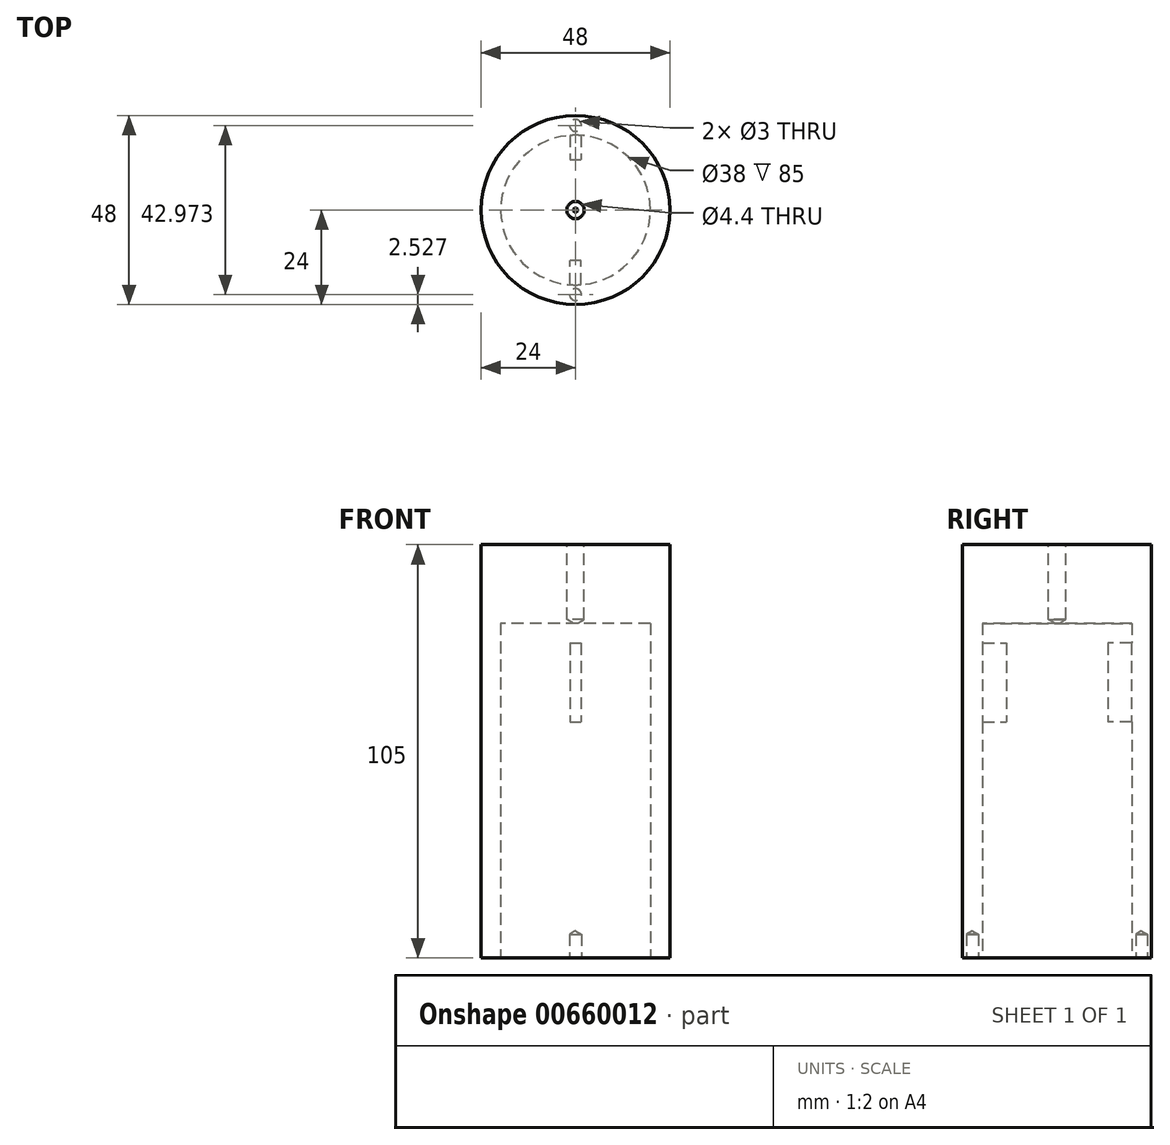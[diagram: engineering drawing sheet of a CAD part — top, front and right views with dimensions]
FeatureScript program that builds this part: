
annotation { "Feature Type Name" : "Feature", "Feature Type Description" : "" }
export const myFeature = defineFeature(function(context is Context, id is Id, definition is map)
    precondition{}
    {
        {
            var Q0;
            Q0=qCreatedBy(makeId("Top.planeOp"),FACE);
            var sketch = newSketch(context, id + "F0", { "sketchPlane" : qUnion([Q0])});
            skCircle(sketch, "E0", {"center": v(0, 0) * mm, "radius": 15.25 * mm});
            skPoint(sketch, "E1", {"position": v(-15.25, 0) * mm});
            skPoint(sketch, "E2", {"position": v(15.25, 0) * mm});
            skArc(sketch, "E3", {"start": v(14.87, 3.38) * mm, "mid": v(18.65, 0) * mm, "end": v(14.87, -3.38) * mm});
            skArc(sketch, "E4", {"start": v(-14.87, 3.38) * mm, "mid": v(-18.65, 0) * mm, "end": v(-14.87, -3.38) * mm});
            skCircle(sketch, "E5", {"center": v(0, 0) * mm, "radius": 19 * mm});
            skCircle(sketch, "E6", {"center": v(0, 0) * mm, "radius": 24 * mm});
            skPoint(sketch, "E7", {"position": v(12.03, 14.7) * mm});
            skPoint(sketch, "E8", {"position": v(-16.68, 9.1) * mm});
            skLineSegment(sketch, "E9", {"start": v(-1.44, -18.95) * mm, "end": v(-1.44, -12.87) * mm});
            skLineSegment(sketch, "E10", {"start": v(-1.44, -12.87) * mm, "end": v(0, -12.87) * mm});
            skLineSegment(sketch, "E11.MirrorCS", {"start": v(1.44, -18.95) * mm, "end": v(1.44, -12.87) * mm});
            skLineSegment(sketch, "E12.MirrorCS", {"start": v(1.44, -12.87) * mm, "end": v(0, -12.87) * mm});
            skLineSegment(sketch, "E13.MirrorCS", {"start": v(-1.44, 18.95) * mm, "end": v(-1.44, 12.87) * mm});
            skLineSegment(sketch, "E14.MirrorCS", {"start": v(-1.44, 12.87) * mm, "end": v(0, 12.87) * mm});
            skLineSegment(sketch, "E15.MirrorCS", {"start": v(1.44, 12.87) * mm, "end": v(0, 12.87) * mm});
            skLineSegment(sketch, "E16.MirrorCS", {"start": v(1.44, 18.95) * mm, "end": v(1.44, 12.87) * mm});
            skPoint(sketch, "E17", {"position": v(0, -18.95) * mm});
            skPoint(sketch, "E18", {"position": v(0, 19) * mm});
            skLineSegment(sketch, "E19", {"start": v(0, -18.95) * mm, "end": v(0, -24) * mm});
            skLineSegment(sketch, "E20", {"start": v(0, 19) * mm, "end": v(0, 24) * mm});
            skPoint(sketch, "E21", {"position": v(0, -21.47) * mm});
            skPoint(sketch, "E22", {"position": v(0, 21.5) * mm});
            skSolve(sketch);
        }
        {
            var Q0;
            Q0=makeQuery(id+"F0.imprint","IMPRINT",FACE,{"disambiguationData":[TD([[makeQuery(id+"F0.imprint","IMPRINT",EDGE,{"derivedFrom":sQuery(id+"F0.wireOp",EDGE,"E6")}),1.0]])]});
            extrude(context, id + "F1", {"entities" : qUnion([Q0]), "depth" : 1 * mm, "offsetDistance" : 25 * mm});
        }
        {
            var Q0;
            Q0=makeQuery(id+"F0.imprint","IMPRINT",FACE,{"disambiguationData":[TD([[makeQuery(id+"F0.imprint","IMPRINT",EDGE,{"derivedFrom":sQuery(id+"F0.wireOp",EDGE,"E5")}),-1.0]])]});
            extrude(context, id + "F2", {"entities" : qUnion([Q0]), "operationType" : NewBodyOperationType.ADD, "depth" : 85 * mm, "offsetDistance" : 25 * mm});
        }
        {
            var Q0;
            {var subQ0=sQuery(id+"F0.wireOp",EDGE,"E3");var subQ1=sQuery(id+"F0.wireOp",EDGE,"E0");var subQ2=makeQuery(id+"F0.imprint","INTERSECT",VERTEX,{"disambiguationData":[OD(0.0)],"derivedFrom":[subQ1,subQ0]});Q0=makeQuery(id+"F0.imprint","IMPRINT",FACE,{"disambiguationData":[TD([[makeQuery(id+"F0.imprint","IMPRINT",EDGE,{"disambiguationData":[TD([[subQ2,-1.0]])],"derivedFrom":subQ1}),1.0]])]});}
            var Q1;
            {var subQ0=sQuery(id+"F0.wireOp",EDGE,"E4");Q1=makeQuery(id+"F0.imprint","IMPRINT",FACE,{"disambiguationData":[TD([[makeQuery(id+"F0.imprint","IMPRINT",EDGE,{"derivedFrom":subQ0}),1.0]])]});}
            var Q2;
            {var subQ0=sQuery(id+"F0.wireOp",EDGE,"E3");Q2=makeQuery(id+"F0.imprint","IMPRINT",FACE,{"disambiguationData":[TD([[makeQuery(id+"F0.imprint","IMPRINT",EDGE,{"derivedFrom":subQ0}),1.0]])]});}
            var Q3;
            Q3=makeQuery(id+"F0.imprint","IMPRINT",FACE,{"disambiguationData":[TD([[makeQuery(id+"F0.imprint","IMPRINT",EDGE,{"derivedFrom":sQuery(id+"F0.wireOp",EDGE,"E5")}),-1.0]])]});
            var Q4;
            {var subQ0=sQuery(id+"F0.wireOp",EDGE,"E3");Q4=makeQuery(id+"F0.imprint","IMPRINT",FACE,{"disambiguationData":[TD([[makeQuery(id+"F0.imprint","IMPRINT",EDGE,{"derivedFrom":subQ0}),-1.0]])]});}
            var Q5;
            {var subQ5=sQuery(id+"F0.wireOp",EDGE,"E4");Q5=makeQuery(id+"F0.imprint","IMPRINT",FACE,{"disambiguationData":[TD([[makeQuery(id+"F0.imprint","IMPRINT",EDGE,{"derivedFrom":subQ5}),-1.0]])]});}
            var Q6;
            {var subQ4=sQuery(id+"F0.wireOp",EDGE,"E10");Q6=makeQuery(id+"F0.imprint","IMPRINT",FACE,{"disambiguationData":[TD([[makeQuery(id+"F0.imprint","IMPRINT",EDGE,{"derivedFrom":subQ4}),-1.0]])]});}
            var Q7;
            {var subQ0=sQuery(id+"F0.wireOp",EDGE,"E9");var subQ1=sQuery(id+"F0.wireOp",EDGE,"E0");var subQ2=makeQuery(id+"F0.imprint","INTERSECT",VERTEX,{"derivedFrom":[subQ1,subQ0]});Q7=makeQuery(id+"F0.imprint","IMPRINT",FACE,{"disambiguationData":[TD([[makeQuery(id+"F0.imprint","IMPRINT",EDGE,{"disambiguationData":[TD([[subQ2,-1.0]])],"derivedFrom":subQ1}),-1.0]])]});}
            var Q8;
            {var subQ0=sQuery(id+"F0.wireOp",EDGE,"E16.MirrorCS");var subQ1=sQuery(id+"F0.wireOp",EDGE,"E0");var subQ2=makeQuery(id+"F0.imprint","INTERSECT",VERTEX,{"derivedFrom":[subQ1,subQ0]});Q8=makeQuery(id+"F0.imprint","IMPRINT",FACE,{"disambiguationData":[TD([[makeQuery(id+"F0.imprint","IMPRINT",EDGE,{"disambiguationData":[TD([[subQ2,-1.0]])],"derivedFrom":subQ1}),-1.0]])]});}
            var Q9;
            {var subQ1=sQuery(id+"F0.wireOp",EDGE,"E14.MirrorCS");Q9=makeQuery(id+"F0.imprint","IMPRINT",FACE,{"disambiguationData":[TD([[makeQuery(id+"F0.imprint","IMPRINT",EDGE,{"derivedFrom":subQ1}),1.0]])]});}
            extrude(context, id + "F3", {"entities" : qUnion([Q0, Q1, Q2, Q3, Q4, Q5, Q6, Q7, Q8, Q9]), "operationType" : NewBodyOperationType.ADD, "depth" : 105 * mm, "offsetDistance" : 25 * mm, "hasSecondDirection" : true, "secondDirectionOppositeDirection" : true, "secondDirectionDepth" : -85 * mm});
        }
        {
            var Q0;
            {var subQ4=sQuery(id+"F0.wireOp",EDGE,"E10");Q0=makeQuery(id+"F0.imprint","IMPRINT",FACE,{"disambiguationData":[TD([[makeQuery(id+"F0.imprint","IMPRINT",EDGE,{"derivedFrom":subQ4}),-1.0]])]});}
            var Q1;
            {var subQ0=sQuery(id+"F0.wireOp",EDGE,"E9");var subQ1=sQuery(id+"F0.wireOp",EDGE,"E0");var subQ2=makeQuery(id+"F0.imprint","INTERSECT",VERTEX,{"derivedFrom":[subQ1,subQ0]});Q1=makeQuery(id+"F0.imprint","IMPRINT",FACE,{"disambiguationData":[TD([[makeQuery(id+"F0.imprint","IMPRINT",EDGE,{"disambiguationData":[TD([[subQ2,-1.0]])],"derivedFrom":subQ1}),-1.0]])]});}
            var Q2;
            {var subQ1=sQuery(id+"F0.wireOp",EDGE,"E14.MirrorCS");Q2=makeQuery(id+"F0.imprint","IMPRINT",FACE,{"disambiguationData":[TD([[makeQuery(id+"F0.imprint","IMPRINT",EDGE,{"derivedFrom":subQ1}),1.0]])]});}
            var Q3;
            {var subQ0=sQuery(id+"F0.wireOp",EDGE,"E16.MirrorCS");var subQ1=sQuery(id+"F0.wireOp",EDGE,"E0");var subQ2=makeQuery(id+"F0.imprint","INTERSECT",VERTEX,{"derivedFrom":[subQ1,subQ0]});Q3=makeQuery(id+"F0.imprint","IMPRINT",FACE,{"disambiguationData":[TD([[makeQuery(id+"F0.imprint","IMPRINT",EDGE,{"disambiguationData":[TD([[subQ2,-1.0]])],"derivedFrom":subQ1}),-1.0]])]});}
            extrude(context, id + "F4", {"entities" : qUnion([Q0, Q1, Q2, Q3]), "operationType" : NewBodyOperationType.ADD, "depth" : 80 * mm, "offsetDistance" : 25 * mm, "hasSecondDirection" : true, "secondDirectionOppositeDirection" : true, "secondDirectionDepth" : -60 * mm});
        }
        {
            var Q0;
            Q0=makeQuery(id+"F3.opExtrude","CAP_FACE",FACE,{"disambiguationData":[OSD([sQuery(id+"F0.wireOp",EDGE,"E6")])],"isStart":false});
            var sketch = newSketch(context, id + "F5", { "sketchPlane" : qUnion([Q0])});
            skPoint(sketch, "E23", {"position": v(0, 0) * mm});
            skSolve(sketch);
        }
        {
            var Q0;
            Q0=sQuery(id+"F5.wireOp",VERTEX,"E23");
            var Q1;
            Q1=makeQuery(id+"F1.opExtrude","SWEPT_BODY",BODY,{"disambiguationData":[OSD([sQuery(id+"F0.wireOp",EDGE,"E0"),sQuery(id+"F0.wireOp",EDGE,"E3"),sQuery(id+"F0.wireOp",EDGE,"E4"),sQuery(id+"F0.wireOp",EDGE,"E6")])]});
            hole(context, id + "F6", {"style" : HoleStyle.SIMPLE, "endStyle" : HoleEndStyle.BLIND, "standardTappedOrClearance" : lookupTablePath({ "standard" : "ISO", "fit" : "Normal", "size" : "M4", "type" : "Clearance" }), "standardBlindInLast" : lookupTablePath({ "fit" : "Standard", "standard" : "ISO", "size" : "M4", "type" : "Clearance" }), "holeDiameter" : 4.4 * mm, "majorDiameter" : 5 * mm, "holeDepth" : 19 * mm, "isTappedThrough" : true, "tappedDepth" : 12 * mm, "tapClearance" : 3, "locations" : qUnion([Q0]), "scope" : qUnion([Q1])});
        }
        {
            var Q0;
            Q0=sQuery(id+"F0.wireOp",VERTEX,"E21");
            var Q1;
            Q1=sQuery(id+"F0.wireOp",VERTEX,"E22");
            var Q2;
            Q2=makeQuery(id+"F1.opExtrude","SWEPT_BODY",BODY,{"disambiguationData":[OSD([sQuery(id+"F0.wireOp",EDGE,"E5"),sQuery(id+"F0.wireOp",EDGE,"E6")])]});
            hole(context, id + "F7", {"style" : HoleStyle.SIMPLE, "endStyle" : HoleEndStyle.BLIND, "oppositeDirection" : true, "holeDiameter" : 3 * mm, "majorDiameter" : 5 * mm, "holeDepth" : 6 * mm, "isTappedThrough" : true, "tappedDepth" : 12 * mm, "tapClearance" : 3, "locations" : qUnion([Q0, Q1]), "scope" : qUnion([Q2])});
        }
    });
